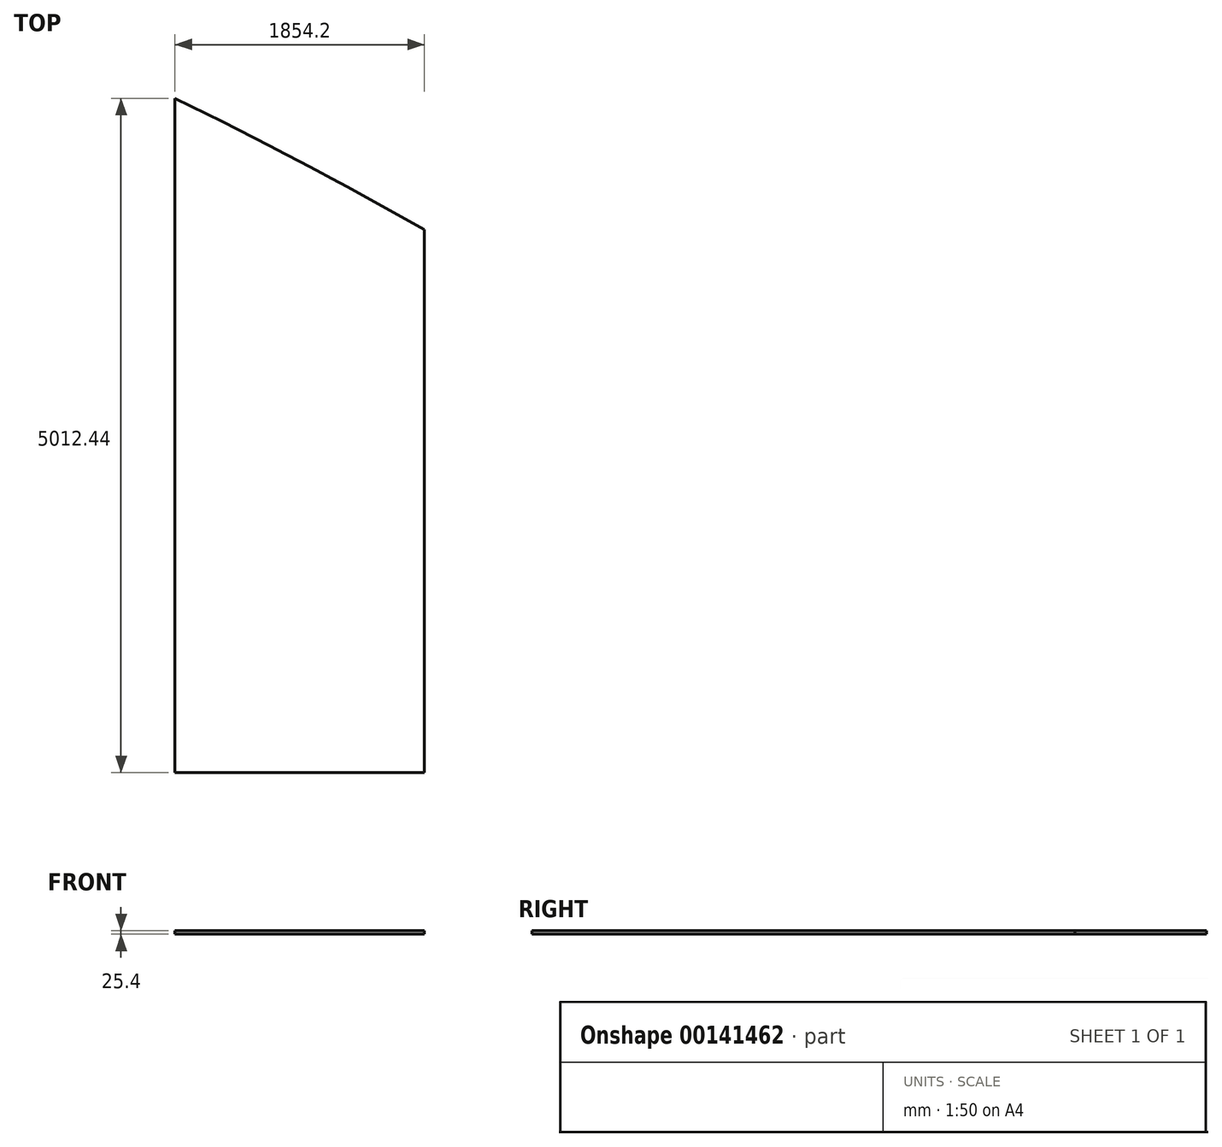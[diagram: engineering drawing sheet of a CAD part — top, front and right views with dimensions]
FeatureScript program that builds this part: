
annotation { "Feature Type Name" : "Feature", "Feature Type Description" : "" }
export const myFeature = defineFeature(function(context is Context, id is Id, definition is map)
    precondition{}
    {
        {
            var Q0;
            Q0=qCreatedBy(makeId("Top.planeOp"),FACE);
            var sketch = newSketch(context, id + "F0", { "sketchPlane" : qUnion([Q0])});
            skLineSegment(sketch, "E0", {"start": v(-930.03, -906.36) * mm, "end": v(924.17, -906.36) * mm});
            skLineSegment(sketch, "E1", {"start": v(-930.03, -906.36) * mm, "end": v(-930.03, 4106.08) * mm});
            skLineSegment(sketch, "E2", {"start": v(924.17, -906.36) * mm, "end": v(924.17, 3128.43) * mm});
            skLineSegment(sketch, "E3", {"start": v(-2.93, -906.36) * mm, "end": v(-2.93, 3635.92) * mm});
            skArc(sketch, "E4", {"start": v(924.17, 3128.43) * mm, "mid": v(4.77, 3631.86) * mm, "end": v(-930.03, 4106.08) * mm});
            skSolve(sketch);
        }
        {
            var Q0;
            {var subQ0=sQuery(id+"F0.wireOp",EDGE,"E1");Q0=makeQuery(id+"F0.imprint","IMPRINT",FACE,{"disambiguationData":[TD([[makeQuery(id+"F0.imprint","IMPRINT",EDGE,{"derivedFrom":subQ0}),-1.0]])]});}
            var Q1;
            {var subQ0=sQuery(id+"F0.wireOp",EDGE,"E2");Q1=makeQuery(id+"F0.imprint","IMPRINT",FACE,{"disambiguationData":[TD([[makeQuery(id+"F0.imprint","IMPRINT",EDGE,{"derivedFrom":subQ0}),1.0]])]});}
            extrude(context, id + "F1", {"entities" : qUnion([Q0, Q1]), "depth" : 25.4 * mm});
        }
    });
